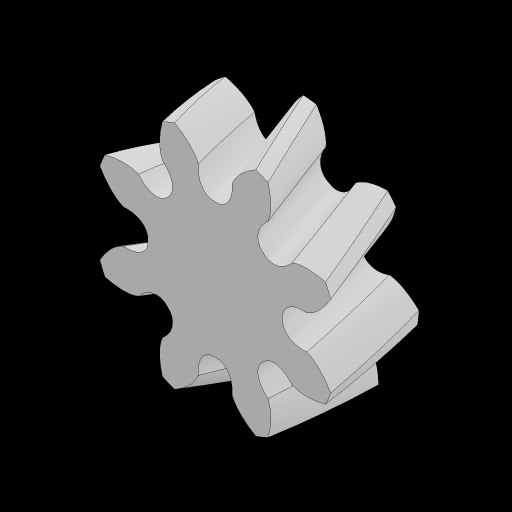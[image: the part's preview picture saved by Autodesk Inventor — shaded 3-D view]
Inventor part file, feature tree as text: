
AUTODESK INVENTOR PART (.ipt)
format: ipt  version: 2023.2 (Build 272271030, 271C)  size: 393,728 bytes
history: native  units: mm
features: sketch x1, extrude x1, helix x1, pattern_circular x1
ambient origin geometry x8: Origin, YZ Plane, XZ Plane, XY Plane, X Axis, Y Axis, Z Axis, Center Point
bodies: Solid1 (feature_tree)
feature tree (4):
  sketch  "Sketch1"  dims[d0=5.0mm d1=0.0mm d2=110.1mm d3=10.0mm d4=10.0mm d5=0.0mm d6=90.0deg d7=90.0deg d8=0.0mm d9=0.0mm d10=80.0mm d11=360.0deg]
  extrude  "Extrusion1"  Depth=80.0mm TaperAngle=360.0deg
  helix  "Coil1"  [1 undecoded]
  pattern_circular  "Circular Pattern1"  [2 undecoded]
note: 3 required parameter values undecoded (feature->parameter linkage not recoverable at this tier; creation-order binding heuristic only, values carry confidence <= 0.55)
